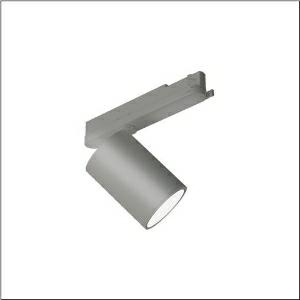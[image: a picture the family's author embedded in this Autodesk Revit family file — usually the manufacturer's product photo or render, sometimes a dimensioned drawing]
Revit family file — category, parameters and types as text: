
# Revit family: spot_31_51sf62mad4b
name_source: partatom
category: Lighting Fixtures
units: mm (PartAtom-declared; Revit-internal decimal feet)

## family parameters
Cut with Voids When Loaded = No
Host = Face
Light Source = No
Part Type = Normal
Room Calculation Point = No
Round Connector Dimension = Use Diameter
Shared = No

## types (1)
- --- (1 x LED, 5140 lm, 41.6 W, 4000K)
    Apparent Load = 42 VA
    CIE Flux Codes = 93 97 99 100 100
    Color Rendering = 90
    Color Temperature = 4000K
    Default Elevation = 1800 mm
    Description = Spot 31, directional spotlight, light control with lens, of PMMA, LED rated luminous flux: 4.930lm, light colour: 940, control gear: ECG Multilumen, with 3-phase adapter, mains connection: 220..240V, AC, 50/60Hz, of aluminium, metallic grey (RAL 9006), length: 213mm, diameter: 90mm, protection rating (complete): IP20, insulation class (complete): insulation class I (protective earthing), certification: CE, impact resistance: IK02, permissible ambient temperature for indoor applications: -20..+40°C, packaging unit: 1 piece
    Height = 175 mm
    Lamp = 1 x LED
    Lamp Light Flux = 5140 lm
    Lamp Power = 41.6 W
    Lamp count = 1
    Length = 90 mm
    Luminous efficacy = 124 lm/W
    Manufacturer = Siteco
    ModVariant = No
    Model = 51SF62MAD4B
    Mounting Place = Ceiling
    Mounting Type = Pendant
    Number of Poles = 1
    OnlyDefault = Yes
    Power Factor = 1
    Product Name = Spot 31
    Product group = directional spotlight
    ProductGroupID = 906
    Protection Class = Protection class I
    Protection Degree = IP 20
    RLX_Detail_Level = 1
    RLX_Emergency_Light_Flux = 0 lm
    RLX_Emergency_Type = 0
    RLX_Emergency_Type_DB = No
    RlxData = <blob elided: 20021 chars, md5=8252d4f7>
    Socket = socket
    Standby Power = 0 W
    System Light Flux = 5140 lm
    System Power = 42 W
    Type Comments = factory setting: luminous flux: 100 % | (ON | ON | ON | ON) | 1050 mA
    Type Image = l_1273725.jpg
    URL = http://relux.com
    VarID = @adj_146538
    Voltage = 0 V
    Weight = 0.00 kg
    Width = 0 mm  [stored 0 ft]

note: [stored X ft] marks values corroborated as IEEE doubles in the binary element streams (Revit-internal decimal feet)

## geometry (parser evidence)
native form markers: Blend x4, Sweep x11
no freeform markers — native parametric forms only
